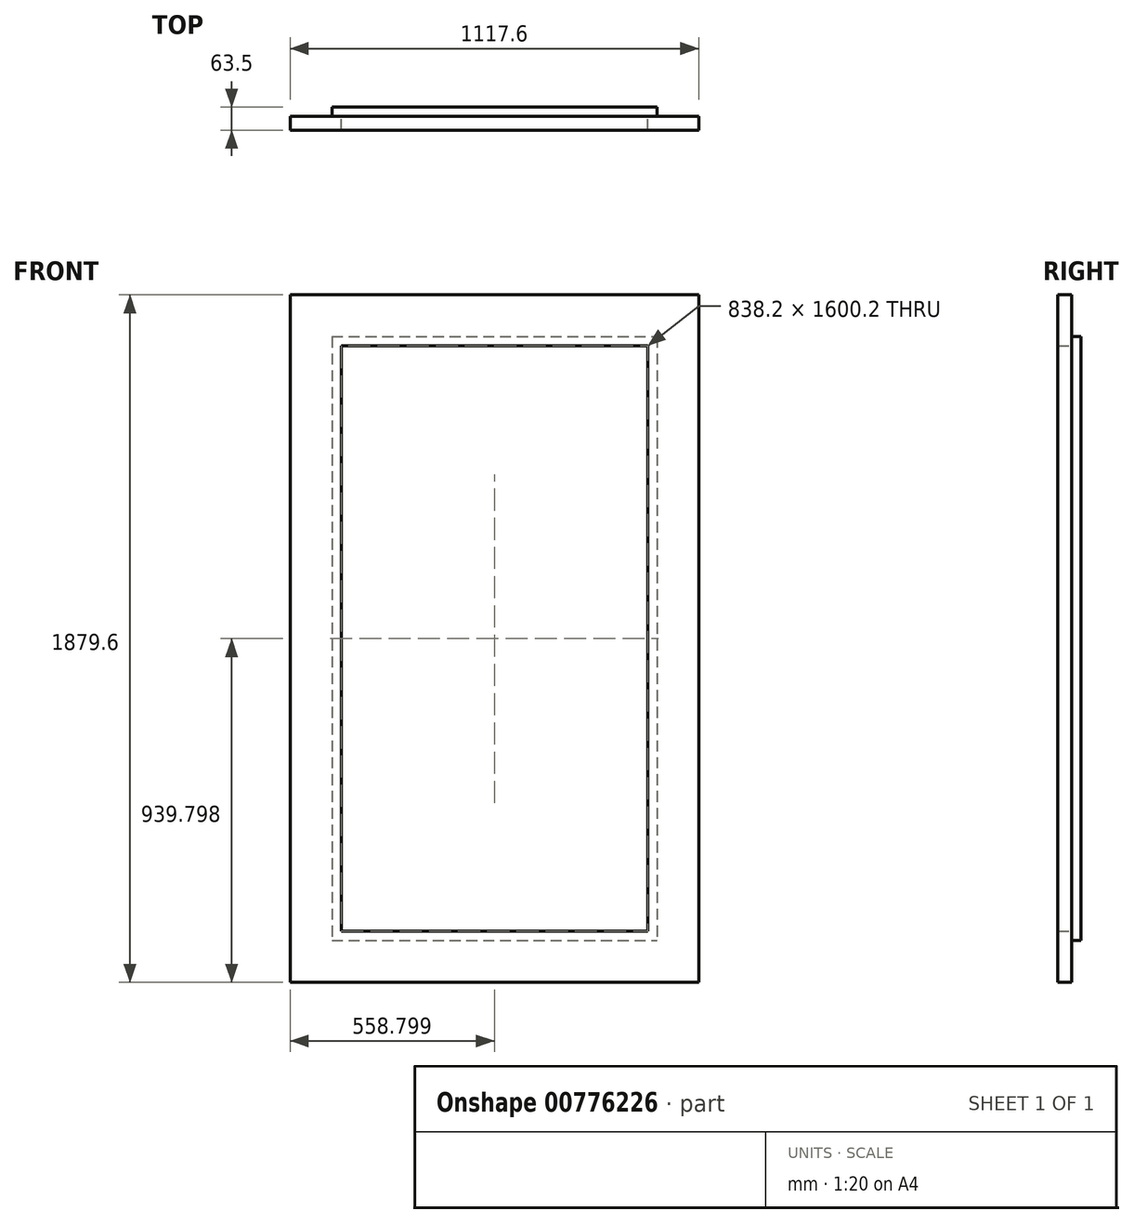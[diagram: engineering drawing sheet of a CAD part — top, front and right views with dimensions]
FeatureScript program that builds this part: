
annotation { "Feature Type Name" : "Feature", "Feature Type Description" : "" }
export const myFeature = defineFeature(function(context is Context, id is Id, definition is map)
    precondition{}
    {
        {
            var Q0;
            Q0=qCreatedBy(makeId("Front.planeOp"),FACE);
            var sketch = newSketch(context, id + "F0", { "sketchPlane" : qUnion([Q0])});
            skLineSegment(sketch, "E0.bottom", {"start": v(-443.61, 1157.52) * mm, "end": v(445.39, 1157.52) * mm});
            skLineSegment(sketch, "E0.top", {"start": v(-443.61, -493.48) * mm, "end": v(445.39, -493.48) * mm});
            skLineSegment(sketch, "E0.left", {"start": v(-443.61, 1157.52) * mm, "end": v(-443.61, -493.48) * mm});
            skLineSegment(sketch, "E0.right", {"start": v(445.39, 1157.52) * mm, "end": v(445.39, -493.48) * mm});
            skSolve(sketch);
        }
        {
            var Q0;
            Q0=makeQuery(id+"F0.imprint","IMPRINT",FACE,{"disambiguationData":[TD([[makeQuery(id+"F0.imprint","IMPRINT",EDGE,{"derivedFrom":sQuery(id+"F0.wireOp",EDGE,"E0.bottom")}),-1.0]])]});
            extrude(context, id + "F1", {"entities" : qUnion([Q0]), "depth" : 25.4 * mm, "offsetDistance" : 25.4 * mm});
        }
        {
            var Q0;
            Q0=makeQuery(id+"F1.opExtrude","CAP_FACE",FACE,{"disambiguationData":[OSD([sQuery(id+"F0.wireOp",EDGE,"E0.bottom"),sQuery(id+"F0.wireOp",EDGE,"E0.top"),sQuery(id+"F0.wireOp",EDGE,"E0.left"),sQuery(id+"F0.wireOp",EDGE,"E0.right")])],"isStart":false});
            var sketch = newSketch(context, id + "F2", { "sketchPlane" : qUnion([Q0])});
            skLineSegment(sketch, "E1.bottom", {"start": v(-557.91, -468.08) * mm, "end": v(559.69, -468.08) * mm});
            skLineSegment(sketch, "E1.top", {"start": v(-557.91, -607.78) * mm, "end": v(559.69, -607.78) * mm});
            skLineSegment(sketch, "E1.left", {"start": v(-557.91, -468.08) * mm, "end": v(-557.91, -607.78) * mm});
            skLineSegment(sketch, "E1.right", {"start": v(559.69, -468.08) * mm, "end": v(559.69, -607.78) * mm});
            skLineSegment(sketch, "E2.bottom", {"start": v(-557.91, 1271.82) * mm, "end": v(559.69, 1271.82) * mm});
            skLineSegment(sketch, "E2.top", {"start": v(-557.91, 1132.12) * mm, "end": v(559.69, 1132.12) * mm});
            skLineSegment(sketch, "E2.left", {"start": v(-557.91, 1271.82) * mm, "end": v(-557.91, 1132.12) * mm});
            skLineSegment(sketch, "E2.right", {"start": v(559.69, 1271.82) * mm, "end": v(559.69, 1132.12) * mm});
            skLineSegment(sketch, "E3.bottom", {"start": v(559.69, 1132.12) * mm, "end": v(419.99, 1132.12) * mm});
            skLineSegment(sketch, "E3.top", {"start": v(559.69, -468.08) * mm, "end": v(419.99, -468.08) * mm});
            skLineSegment(sketch, "E3.left", {"start": v(559.69, 1132.12) * mm, "end": v(559.69, -468.08) * mm});
            skLineSegment(sketch, "E3.right", {"start": v(419.99, 1132.12) * mm, "end": v(419.99, -468.08) * mm});
            skLineSegment(sketch, "E4.bottom", {"start": v(-557.91, 1132.12) * mm, "end": v(-418.21, 1132.12) * mm});
            skLineSegment(sketch, "E4.top", {"start": v(-557.91, -468.08) * mm, "end": v(-418.21, -468.08) * mm});
            skLineSegment(sketch, "E4.left", {"start": v(-557.91, 1132.12) * mm, "end": v(-557.91, -468.08) * mm});
            skLineSegment(sketch, "E4.right", {"start": v(-418.21, 1132.12) * mm, "end": v(-418.21, -468.08) * mm});
            skSolve(sketch);
        }
        {
            var Q0;
            Q0 = qSketchRegion(id + "F2", true);
            extrude(context, id + "F3", {"entities" : qUnion([Q0]), "depth" : 38.1 * mm, "offsetDistance" : 25.4 * mm});
        }
    });
